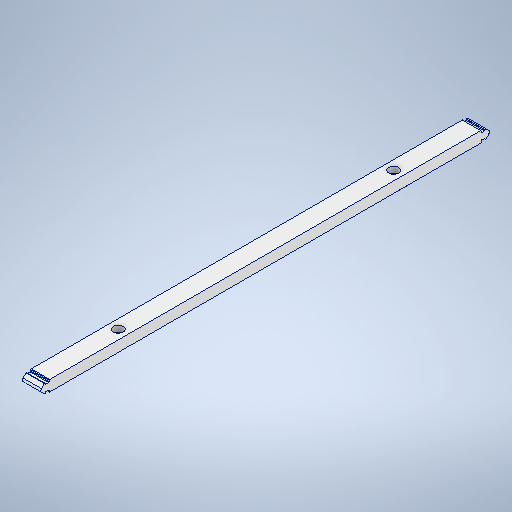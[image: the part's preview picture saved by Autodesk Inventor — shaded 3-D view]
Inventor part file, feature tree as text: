
AUTODESK INVENTOR PART (.ipt)
format: ipt  version: 2025 (Build 290162000, 162)  size: 306,688 bytes
history: native  units: mm
features: sketch x3, extrude x2, fillet x2, mirror x1, hole x1
ambient origin geometry x8: Origin, YZ Plane, XZ Plane, XY Plane, X Axis, Y Axis, Z Axis, Center Point
bodies: Solid1 (feature_tree)
feature tree (9):
  extrude  "Extrusion1"  Depth=10.0mm
  extrude  "Extrusion2"  Depth=6.0mm
  fillet  "Fillet1"  Radius=3.5mm
  fillet  "Fillet2"  Radius=5.0mm
  mirror  "Mirror2"
  hole  "Hole1"  [1 undecoded]
  sketch  "Sketch1"  dims[d0=17.0mm d1=10.0mm]
  sketch  "Sketch2"  dims[d2=207.8mm d3=0.0mm d5=6.0mm d6=3.5mm d7=5.0mm]
  sketch  "Sketch3"  dims[d8=0.0mm d9=0.0mm d10=0.5mm d11=2.0mm d12=254.0mm d13=127.0mm d14=9.0mm d15=16.0mm d16=17.3mm d17=2.0mm d18=90.0deg d19=8.0mm d20=20.594885mm]
note: 1 required parameter value undecoded (feature->parameter linkage not recoverable at this tier; creation-order binding heuristic only, values carry confidence <= 0.55)
